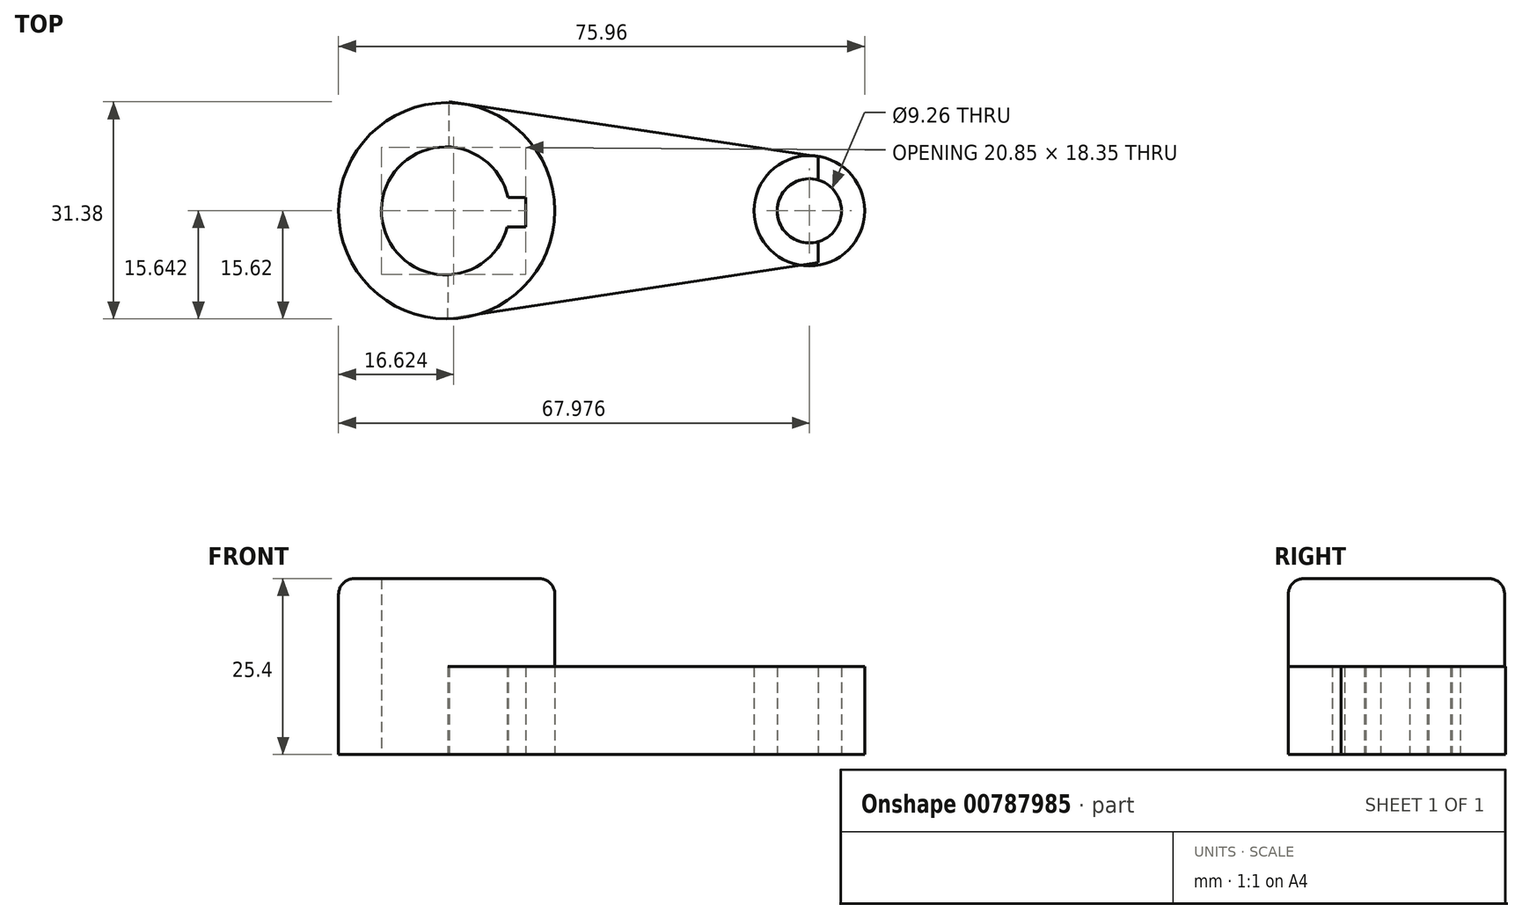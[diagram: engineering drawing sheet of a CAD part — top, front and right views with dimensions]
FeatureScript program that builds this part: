
annotation { "Feature Type Name" : "Feature", "Feature Type Description" : "" }
export const myFeature = defineFeature(function(context is Context, id is Id, definition is map)
    precondition{}
    {
        {
            var Q0;
            Q0=qCreatedBy(makeId("Top.planeOp"),FACE);
            var sketch = newSketch(context, id + "F0", { "sketchPlane" : qUnion([Q0])});
            skCircle(sketch, "E0", {"center": v(17.6, 0) * mm, "radius": 7.98 * mm});
            skCircle(sketch, "E1", {"center": v(-34.75, 0) * mm, "radius": 15.62 * mm});
            skSolve(sketch);
        }
        {
            var Q0;
            Q0=qCreatedBy(makeId("Top.planeOp"),FACE);
            var sketch = newSketch(context, id + "F1", { "sketchPlane" : qUnion([Q0])});
            skLineSegment(sketch, "E2", {"start": v(-34.38, 15.76) * mm, "end": v(18.9, 7.84) * mm});
            skLineSegment(sketch, "E3", {"start": v(18.9, 7.84) * mm, "end": v(18.9, -7.47) * mm});
            skLineSegment(sketch, "E4", {"start": v(18.9, -7.47) * mm, "end": v(-34.57, -15.58) * mm});
            skLineSegment(sketch, "E5", {"start": v(-34.57, -15.58) * mm, "end": v(-34.38, 15.76) * mm});
            skSolve(sketch);
        }
        {
            var Q0;
            Q0=makeQuery(id+"F0.imprint","IMPRINT",FACE,{"disambiguationData":[TD([[makeQuery(id+"F0.imprint","IMPRINT",EDGE,{"derivedFrom":sQuery(id+"F0.wireOp",EDGE,"E1")}),1.0]])]});
            extrude(context, id + "F2", {"entities" : qUnion([Q0]), "depth" : 25.4 * mm, "offsetDistance" : 25.4 * mm});
        }
        {
            var Q0;
            Q0=makeQuery(id+"F0.imprint","IMPRINT",FACE,{"disambiguationData":[TD([[makeQuery(id+"F0.imprint","IMPRINT",EDGE,{"derivedFrom":sQuery(id+"F0.wireOp",EDGE,"E0")}),1.0]])]});
            extrude(context, id + "F3", {"entities" : qUnion([Q0]), "depth" : 12.7 * mm, "offsetDistance" : 25.4 * mm});
        }
        {
            var Q0;
            Q0=makeQuery(id+"F1.imprint","IMPRINT",FACE,{"disambiguationData":[TD([[makeQuery(id+"F1.imprint","IMPRINT",EDGE,{"derivedFrom":sQuery(id+"F1.wireOp",EDGE,"E2")}),-1.0]])]});
            extrude(context, id + "F4", {"entities" : qUnion([Q0]), "depth" : 12.7 * mm, "offsetDistance" : 25.4 * mm});
        }
        {
            var Q0;
            Q0=qCreatedBy(makeId("Top.planeOp"),FACE);
            var sketch = newSketch(context, id + "F5", { "sketchPlane" : qUnion([Q0])});
            skCircle(sketch, "E6", {"center": v(17.6, 0) * mm, "radius": 4.63 * mm});
            skSolve(sketch);
        }
        {
            var Q0;
            Q0 = qSketchRegion(id + "F5", true);
            extrude(context, id + "F6", {"entities" : qUnion([Q0]), "operationType" : NewBodyOperationType.REMOVE, "depth" : 12.7 * mm, "offsetDistance" : 25.4 * mm});
        }
        {
            var Q0;
            Q0=qCreatedBy(makeId("Top.planeOp"),FACE);
            var sketch = newSketch(context, id + "F7", { "sketchPlane" : qUnion([Q0])});
            skCircle(sketch, "E7", {"center": v(-34.94, 0) * mm, "radius": 9.24 * mm});
            skSolve(sketch);
        }
        {
            var Q0;
            Q0 = qSketchRegion(id + "F7", true);
            extrude(context, id + "F8", {"entities" : qUnion([Q0]), "operationType" : NewBodyOperationType.REMOVE, "depth" : 25.4 * mm, "offsetDistance" : 25.4 * mm});
        }
        {
            var Q0;
            Q0=qCreatedBy(makeId("Top.planeOp"),FACE);
            var sketch = newSketch(context, id + "F9", { "sketchPlane" : qUnion([Q0])});
            skLineSegment(sketch, "E8.bottom", {"start": v(-28.67, 1.94) * mm, "end": v(-23.32, 1.94) * mm});
            skLineSegment(sketch, "E8.top", {"start": v(-28.67, -2.3) * mm, "end": v(-23.32, -2.3) * mm});
            skLineSegment(sketch, "E8.left", {"start": v(-28.67, 1.94) * mm, "end": v(-28.67, -2.3) * mm});
            skLineSegment(sketch, "E8.right", {"start": v(-23.32, 1.94) * mm, "end": v(-23.32, -2.3) * mm});
            skSolve(sketch);
        }
        {
            var Q0;
            Q0 = qSketchRegion(id + "F9", true);
            extrude(context, id + "F10", {"entities" : qUnion([Q0]), "operationType" : NewBodyOperationType.REMOVE, "depth" : 25.4 * mm, "offsetDistance" : 25.4 * mm});
        }
        {
            var Q0;
            Q0=makeQuery(id+"F2.opExtrude","CAP_EDGE",EDGE,{"disambiguationData":[OSD([sQuery(id+"F0.wireOp",EDGE,"E1")])],"isStart":false});
            fillet(context, id + "F11", {"entities" : qUnion([Q0]), "radius" : 2.3 * mm, "tangentPropagation" : true, "allowEdgeOverflow" : false});
        }
    });
